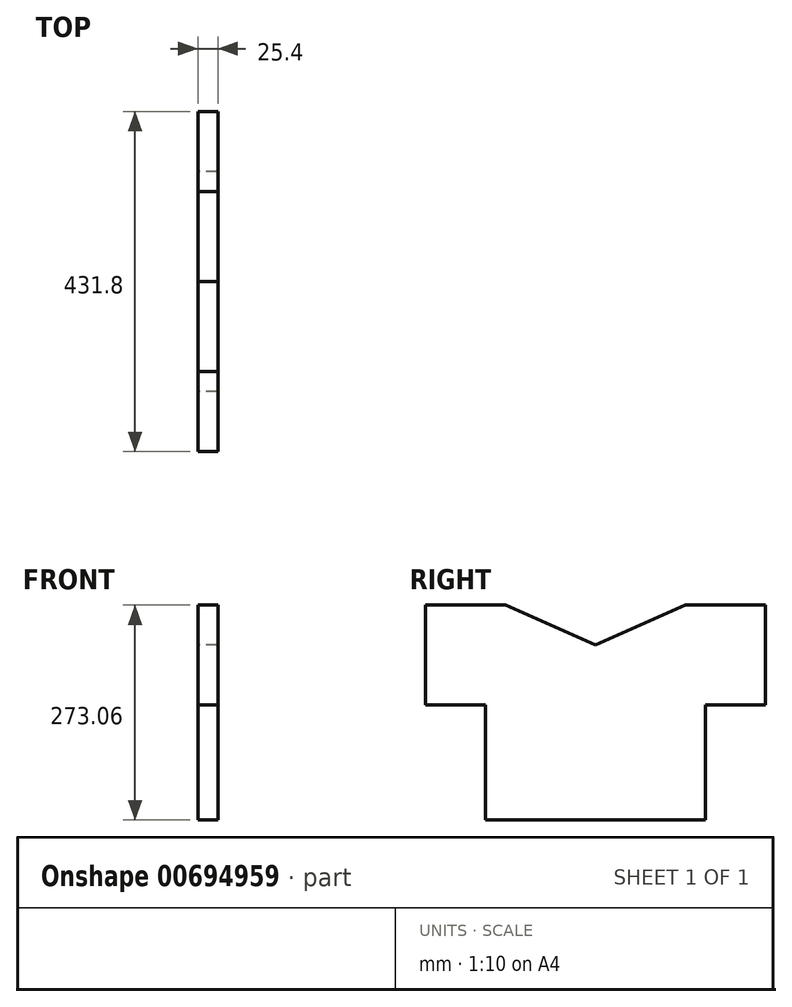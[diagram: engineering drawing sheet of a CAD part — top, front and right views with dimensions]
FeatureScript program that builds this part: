
annotation { "Feature Type Name" : "Feature", "Feature Type Description" : "" }
export const myFeature = defineFeature(function(context is Context, id is Id, definition is map)
    precondition{}
    {
        {
            var Q0;
            Q0=qCreatedBy(makeId("Right.planeOp"),FACE);
            var sketch = newSketch(context, id + "F0", { "sketchPlane" : qUnion([Q0])});
            skLineSegment(sketch, "E0.bottom", {"start": v(-215.9, 136.53) * mm, "end": v(-114.3, 136.53) * mm});
            skLineSegment(sketch, "E0.top", {"start": v(-139.7, -136.53) * mm, "end": v(139.7, -136.53) * mm});
            skLineSegment(sketch, "E0.left", {"start": v(-215.9, 136.53) * mm, "end": v(-215.9, 9.53) * mm});
            skLineSegment(sketch, "E0.right", {"start": v(215.9, 136.53) * mm, "end": v(215.9, 9.52) * mm});
            skPoint(sketch, "E0.middle", {"position": v(0, 0) * mm});
            skLineSegment(sketch, "E1", {"start": v(0, 195.24) * mm, "end": v(0, -224.07) * mm, "construction": true});
            skLineSegment(sketch, "E2.0", {"start": v(-215.9, 9.53) * mm, "end": v(-139.7, 9.53) * mm});
            skLineSegment(sketch, "E3.MirrorCS", {"start": v(139.7, 9.53) * mm, "end": v(139.7, -136.53) * mm});
            skPoint(sketch, "E4.orphan", {"position": v(-139.7, -224.07) * mm});
            skPoint(sketch, "E5.orphan", {"position": v(-215.9, -136.53) * mm});
            skPoint(sketch, "E6.orphan", {"position": v(215.9, -136.53) * mm});
            skPoint(sketch, "E7.orphan", {"position": v(139.7, -224.07) * mm});
            skLineSegment(sketch, "E8.trimOffspring", {"start": v(139.7, 9.53) * mm, "end": v(215.9, 9.53) * mm});
            skLineSegment(sketch, "E9.trimOffspring", {"start": v(-139.7, 9.52) * mm, "end": v(-139.7, -136.53) * mm});
            skPoint(sketch, "E10.0.start.orphan", {"position": v(-139.7, 195.24) * mm});
            skPoint(sketch, "E11.orphan", {"position": v(139.7, 195.24) * mm});
            skLineSegment(sketch, "E12.0", {"start": v(-215.9, 85.72) * mm, "end": v(215.9, 85.72) * mm, "construction": true});
            skLineSegment(sketch, "E13.0", {"start": v(-114.3, 195.24) * mm, "end": v(-114.3, -224.07) * mm, "construction": true});
            skLineSegment(sketch, "E14", {"start": v(-114.3, 136.53) * mm, "end": v(0, 85.72) * mm});
            skLineSegment(sketch, "E15.MirrorCS", {"start": v(114.3, 136.53) * mm, "end": v(0, 85.72) * mm});
            skLineSegment(sketch, "E16.trimOffspring", {"start": v(114.3, 136.53) * mm, "end": v(215.9, 136.53) * mm});
            skSolve(sketch);
        }
        {
            var Q0;
            Q0 = qSketchRegion(id + "F0", true);
            extrude(context, id + "F1", {"entities" : qUnion([Q0]), "depth" : 25.4 * mm, "offsetDistance" : 25.4 * mm});
        }
    });
